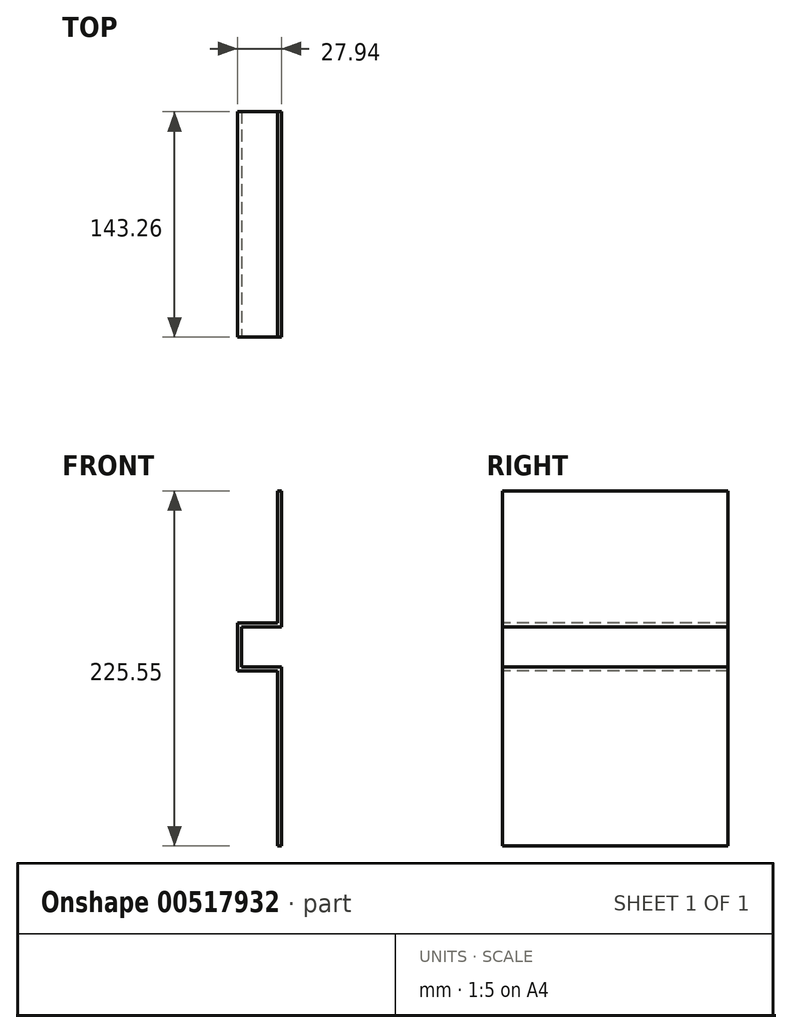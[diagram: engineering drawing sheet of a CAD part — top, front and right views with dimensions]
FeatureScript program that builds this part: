
annotation { "Feature Type Name" : "Feature", "Feature Type Description" : "" }
export const myFeature = defineFeature(function(context is Context, id is Id, definition is map)
    precondition{}
    {
        {
            var Q0;
            Q0=qCreatedBy(makeId("Front.planeOp"),FACE);
            var sketch = newSketch(context, id + "F0", { "sketchPlane" : qUnion([Q0])});
            skLineSegment(sketch, "E0", {"start": v(-20.5, 204.17) * mm, "end": v(-20.5, -21.38) * mm});
            skLineSegment(sketch, "E1", {"start": v(-20.5, -21.38) * mm, "end": v(-17.95, -21.38) * mm});
            skLineSegment(sketch, "E2", {"start": v(-17.95, -21.38) * mm, "end": v(-17.95, 204.17) * mm});
            skLineSegment(sketch, "E3", {"start": v(-17.95, 204.17) * mm, "end": v(-20.5, 204.17) * mm});
            skSolve(sketch);
        }
        {
            var Q0;
            Q0=makeQuery(id+"F0.imprint","IMPRINT",FACE,{"disambiguationData":[TD([[makeQuery(id+"F0.imprint","IMPRINT",EDGE,{"derivedFrom":sQuery(id+"F0.wireOp",EDGE,"E0")}),1.0]])]});
            extrude(context, id + "F1", {"entities" : qUnion([Q0]), "depth" : 143.26 * mm, "offsetDistance" : 25.4 * mm});
        }
        {
            var Q0;
            Q0=makeQuery(id+"F1.opExtrude","CAP_FACE",FACE,{"disambiguationData":[OSD([sQuery(id+"F0.wireOp",EDGE,"E0"),sQuery(id+"F0.wireOp",EDGE,"E1"),sQuery(id+"F0.wireOp",EDGE,"E2"),sQuery(id+"F0.wireOp",EDGE,"E3")])],"isStart":false});
            var sketch = newSketch(context, id + "F2", { "sketchPlane" : qUnion([Q0])});
            skLineSegment(sketch, "E4", {"start": v(-20.5, 120.35) * mm, "end": v(-45.9, 120.35) * mm});
            skLineSegment(sketch, "E5", {"start": v(-45.9, 120.35) * mm, "end": v(-45.9, 89.87) * mm});
            skLineSegment(sketch, "E6", {"start": v(-45.9, 89.87) * mm, "end": v(-20.5, 89.87) * mm});
            skSolve(sketch);
        }
        {
            var Q0;
            {var subQ0=sQuery(id+"F2.wireOp",EDGE,"E4");Q0=makeQuery(id+"F2.imprint","IMPRINT",FACE,{"disambiguationData":[TD([[makeQuery(id+"F2.imprint","IMPRINT",EDGE,{"derivedFrom":subQ0}),1.0]])]});}
            extrude(context, id + "F3", {"entities" : qUnion([Q0]), "operationType" : NewBodyOperationType.ADD, "oppositeDirection" : true, "depth" : 143.26 * mm, "offsetDistance" : 25.4 * mm});
        }
        {
            var Q0;
            {var subQ0=sQuery(id+"F0.wireOp",EDGE,"E0");Q0=makeQuery(id+"F3.boolean.opBoolean","MERGE",FACE,{"derivedFrom":[makeQuery(id+"F1.opExtrude","CAP_FACE",FACE,{"disambiguationData":[OSD([subQ0,sQuery(id+"F0.wireOp",EDGE,"E1"),sQuery(id+"F0.wireOp",EDGE,"E2"),sQuery(id+"F0.wireOp",EDGE,"E3")])],"isStart":false}),makeQuery(id+"F3.opExtrude","CAP_FACE",FACE,{"disambiguationData":[OSD([subQ0,sQuery(id+"F2.wireOp",EDGE,"E4"),sQuery(id+"F2.wireOp",EDGE,"E5"),sQuery(id+"F2.wireOp",EDGE,"E6")])],"isStart":true})]});}
            var sketch = newSketch(context, id + "F4", { "sketchPlane" : qUnion([Q0])});
            skLineSegment(sketch, "E7", {"start": v(-17.95, 117.81) * mm, "end": v(-43.35, 117.81) * mm});
            skLineSegment(sketch, "E8", {"start": v(-43.35, 117.81) * mm, "end": v(-43.35, 92.41) * mm});
            skLineSegment(sketch, "E9", {"start": v(-43.35, 92.41) * mm, "end": v(-17.95, 92.41) * mm});
            skSolve(sketch);
        }
        {
            var Q0;
            {var subQ0=sQuery(id+"F4.wireOp",EDGE,"E7");Q0=makeQuery(id+"F4.imprint","IMPRINT",FACE,{"disambiguationData":[TD([[makeQuery(id+"F4.imprint","IMPRINT",EDGE,{"derivedFrom":subQ0}),1.0]])]});}
            extrude(context, id + "F5", {"entities" : qUnion([Q0]), "operationType" : NewBodyOperationType.REMOVE, "oppositeDirection" : true, "depth" : 177.8 * mm, "offsetDistance" : 25.4 * mm});
        }
    });
